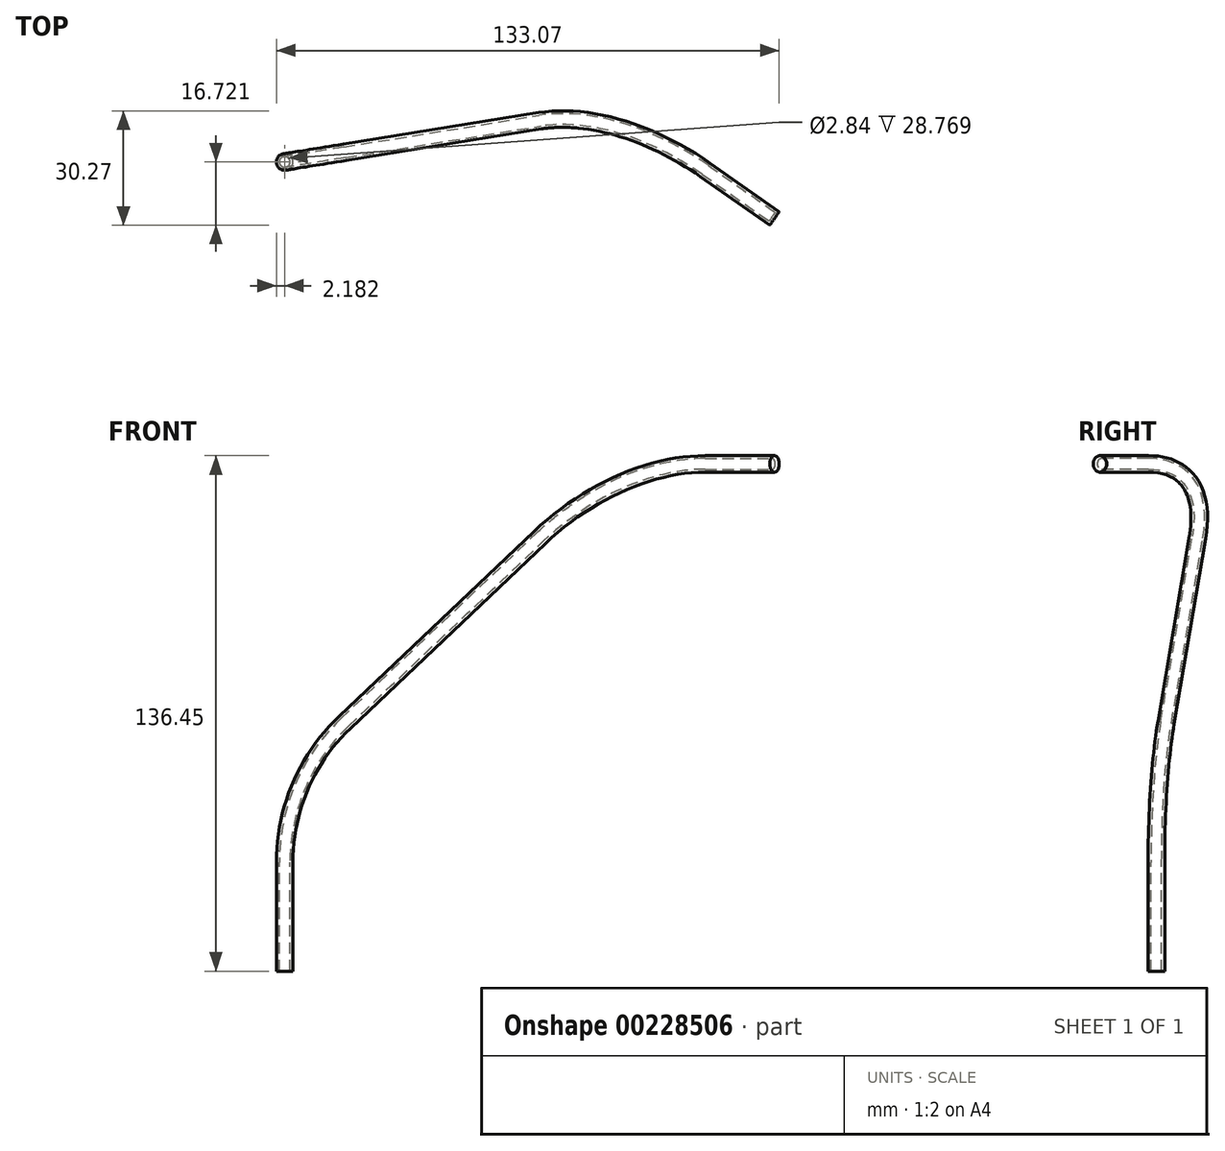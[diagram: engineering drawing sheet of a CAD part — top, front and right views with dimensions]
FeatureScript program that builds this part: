
annotation { "Feature Type Name" : "Feature", "Feature Type Description" : "" }
export const myFeature = defineFeature(function(context is Context, id is Id, definition is map)
    precondition{}
    {
        {
            var Q0;
            Q0=qCreatedBy(makeId("Top.planeOp"),FACE);
            var sketch = newSketch(context, id + "F0", { "sketchPlane" : qUnion([Q0])});
            skLineSegment(sketch, "E0.MirrorCS", {"start": v(32.86, 0) * mm, "end": v(32.86, 282.94) * mm});
            skLineSegment(sketch, "E1.MirrorCS", {"start": v(32.86, 282.94) * mm, "end": v(58.26, 282.94) * mm});
            skLineSegment(sketch, "E2.MirrorCS", {"start": v(0, 0) * mm, "end": v(162.5, 0) * mm});
            skLineSegment(sketch, "E3.MirrorCS", {"start": v(162.5, 0) * mm, "end": v(162.5, 268.01) * mm});
            skLineSegment(sketch, "E4.MirrorCS", {"start": v(162.5, 268.01) * mm, "end": v(187.9, 268.01) * mm});
            skPoint(sketch, "E5.end.orphan", {"position": v(-58.26, 282.94) * mm});
            skPoint(sketch, "E6.end.orphan", {"position": v(-32.86, 282.94) * mm});
            skPoint(sketch, "E7.end.orphan", {"position": v(-187.9, 268.01) * mm});
            skPoint(sketch, "E8.end.orphan", {"position": v(-162.5, 268.01) * mm});
            skPoint(sketch, "E9.orphan", {"position": v(-162.5, 0) * mm});
            skSolve(sketch);
        }
        {
            var Q0;
            Q0=sQuery(id+"F0.wireOp",EDGE,"E4.MirrorCS");
            cPlane(context, id + "F1", {"entities" : qUnion([Q0]), "cplaneType" : CPlaneType.LINE_ANGLE, "offset" : 25.4 * mm, "angle" : 0 * degree, "width" : 152.4 * mm, "height" : 152.4 * mm});
        }
        {
            var Q0;
            Q0=sQuery(id+"F0.wireOp",EDGE,"E1.MirrorCS");
            cPlane(context, id + "F2", {"entities" : qUnion([Q0]), "cplaneType" : CPlaneType.LINE_ANGLE, "offset" : 25.4 * mm, "angle" : 0 * degree, "width" : 152.4 * mm, "height" : 152.4 * mm});
        }
        {
            var Q0;
            Q0=qCreatedBy(id+"F2.planeOp",FACE);
            var sketch = newSketch(context, id + "F3", { "sketchPlane" : qUnion([Q0])});
            skLineSegment(sketch, "E10", {"start": v(-32.86, 0) * mm, "end": v(-32.86, -791.52) * mm});
            skLineSegment(sketch, "E11", {"start": v(-32.86, -791.52) * mm, "end": v(-7.46, -791.52) * mm});
            skSolve(sketch);
        }
        {
            var Q0;
            Q0=qCreatedBy(id+"F1.planeOp",FACE);
            var sketch = newSketch(context, id + "F4", { "sketchPlane" : qUnion([Q0])});
            skLineSegment(sketch, "E12", {"start": v(-162.5, 0) * mm, "end": v(-162.5, -657.26) * mm});
            skLineSegment(sketch, "E13", {"start": v(-162.5, -657.26) * mm, "end": v(-187.9, -657.26) * mm});
            skSolve(sketch);
        }
        {
            var Q0;
            Q0=sQuery(id+"F3.wireOp",EDGE,"E11");
            cPlane(context, id + "F5", {"entities" : qUnion([Q0]), "cplaneType" : CPlaneType.LINE_ANGLE, "offset" : 25.4 * mm, "angle" : 90 * degree, "width" : 152.4 * mm, "height" : 152.4 * mm});
        }
        {
            var Q0;
            Q0=qCreatedBy(id+"F5.planeOp",FACE);
            var sketch = newSketch(context, id + "F6", { "sketchPlane" : qUnion([Q0])});
            skCircle(sketch, "E14", {"center": v(32.86, 282.94) * mm, "radius": 2.18 * mm});
            skSolve(sketch);
        }
        {
            var Q0;
            Q0=sQuery(id+"F4.wireOp",EDGE,"E13");
            cPlane(context, id + "F7", {"entities" : qUnion([Q0]), "cplaneType" : CPlaneType.LINE_ANGLE, "offset" : 25.4 * mm, "angle" : 90 * degree, "width" : 152.4 * mm, "height" : 152.4 * mm});
        }
        {
            var Q0;
            Q0=qCreatedBy(id+"F7.planeOp",FACE);
            var sketch = newSketch(context, id + "F8", { "sketchPlane" : qUnion([Q0])});
            skLineSegment(sketch, "E15", {"start": v(162.5, 268.01) * mm, "end": v(177.07, 288.82) * mm});
            skSolve(sketch);
        }
        {
            var Q0;
            Q0=sQuery(id+"F8.wireOp",EDGE,"E15");
            cPlane(context, id + "F9", {"entities" : qUnion([Q0]), "cplaneType" : CPlaneType.LINE_ANGLE, "offset" : 25.4 * mm, "angle" : 90 * degree, "width" : 152.4 * mm, "height" : 152.4 * mm});
        }
        {
            var Q0;
            Q0=qCreatedBy(id+"F9.planeOp",FACE);
            var sketch = newSketch(context, id + "F10", { "sketchPlane" : qUnion([Q0])});
            skCircle(sketch, "E16", {"center": v(312.75, -657.26) * mm, "radius": 2.18 * mm});
            skSolve(sketch);
        }
        {
            var Q0;
            Q0=qCreatedBy(id+"F7.planeOp",FACE);
            var sketch = newSketch(context, id + "F11", { "sketchPlane" : qUnion([Q0])});
            skLineSegment(sketch, "E17", {"start": v(162.5, 268.01) * mm, "end": v(120.88, 297.15) * mm});
            skSolve(sketch);
        }
        {
            var Q0;
            Q0=sQuery(id+"F3.wireOp",EDGE,"E11");
            var Q1;
            Q1=sQuery(id+"F3.wireOp",EDGE,"E10");
            cPlane(context, id + "F12", {"entities" : qUnion([Q0, Q1]), "cplaneType" : CPlaneType.LINE_ANGLE, "offset" : 25.4 * mm, "angle" : 0 * degree, "width" : 152.4 * mm, "height" : 152.4 * mm});
        }
        {
            var Q0;
            Q0=qCreatedBy(id+"F12.planeOp",FACE);
            var sketch = newSketch(context, id + "F13", { "sketchPlane" : qUnion([Q0])});
            skLineSegment(sketch, "E18", {"start": v(32.86, -791.52) * mm, "end": v(32.86, -740.72) * mm});
            skSolve(sketch);
        }
        {
            var Q0;
            Q0=sQuery(id+"F11.wireOp",VERTEX,"E17.start");
            var Q1;
            Q1=sQuery(id+"F11.wireOp",VERTEX,"E17.end");
            var Q2;
            Q2=sQuery(id+"F13.wireOp",VERTEX,"E18.end");
            cPlane(context, id + "F14", {"entities" : qUnion([Q0, Q1, Q2]), "cplaneType" : CPlaneType.THREE_POINT, "offset" : 25.4 * mm, "width" : 152.4 * mm, "height" : 152.4 * mm});
        }
        {
            var Q0;
            Q0=qCreatedBy(id+"F14.planeOp",FACE);
            var sketch = newSketch(context, id + "F15", { "sketchPlane" : qUnion([Q0])});
            skLineSegment(sketch, "E19", {"start": v(296.36, -357.9) * mm, "end": v(220.28, -303.17) * mm});
            skLineSegment(sketch, "E20", {"start": v(171.02, -297.54) * mm, "end": v(150.36, -306.18) * mm});
            skPoint(sketch, "E21.visualSharp", {"position": v(197.23, -286.58) * mm});
            skArc(sketch, "E21.filletArc", {"start": v(220.28, -303.17) * mm, "mid": v(196.39, -293.94) * mm, "end": v(171.02, -297.54) * mm});
            skSolve(sketch);
        }
        {
            var Q0;
            Q0=sQuery(id+"F13.wireOp",EDGE,"E18");
            var Q1;
            Q1=sQuery(id+"F15.wireOp",EDGE,"E19");
            cPlane(context, id + "F16", {"entities" : qUnion([Q0, Q1]), "cplaneType" : CPlaneType.LINE_ANGLE, "offset" : 25.4 * mm, "angle" : 0 * degree, "width" : 152.4 * mm, "height" : 152.4 * mm});
        }
        {
            var Q0;
            Q0=qCreatedBy(id+"F16.planeOp",FACE);
            var sketch = newSketch(context, id + "F17", { "sketchPlane" : qUnion([Q0])});
            skLineSegment(sketch, "E22", {"start": v(-93.61, -725.66) * mm, "end": v(-145.95, -676.67) * mm});
            skLineSegment(sketch, "E23", {"start": v(-77.53, -762.75) * mm, "end": v(-77.53, -791.52) * mm});
            skPoint(sketch, "E24.visualSharp", {"position": v(-77.53, -740.72) * mm});
            skArc(sketch, "E24.filletArc", {"start": v(-77.53, -762.75) * mm, "mid": v(-81.72, -742.54) * mm, "end": v(-93.61, -725.66) * mm});
            skSolve(sketch);
        }
        {
            var Q0;
            Q0=makeQuery(id+"F6.imprint","IMPRINT",FACE,{"disambiguationData":[TD([[makeQuery(id+"F6.imprint","IMPRINT",EDGE,{"derivedFrom":sQuery(id+"F6.wireOp",EDGE,"E14")}),1.0]])]});
            var Q1;
            Q1=sQuery(id+"F17.wireOp",EDGE,"E23");
            var Q2;
            Q2=sQuery(id+"F17.wireOp",EDGE,"E24.filletArc");
            var Q3;
            Q3=sQuery(id+"F17.wireOp",EDGE,"E22");
            var Q4;
            Q4=sQuery(id+"F15.wireOp",EDGE,"E21.filletArc");
            var Q5;
            Q5=sQuery(id+"F15.wireOp",EDGE,"E20");
            sweep(context, id + "F18", {"profiles" : qUnion([Q0]), "path" : qUnion([Q1, Q2, Q3, Q4, Q5])});
        }
        {
            var Q0;
            Q0=makeQuery(id+"F18.opSweep","CAP_FACE",FACE,{"disambiguationData":[OSD([sQuery(id+"F6.wireOp",EDGE,"E14"),sQuery(id+"F17.wireOp",VERTEX,"E23.end")])],"isStart":true});
            shell(context, id + "F19", {"entities" : qUnion([Q0]), "thickness" : 0.76 * mm});
        }
    });
